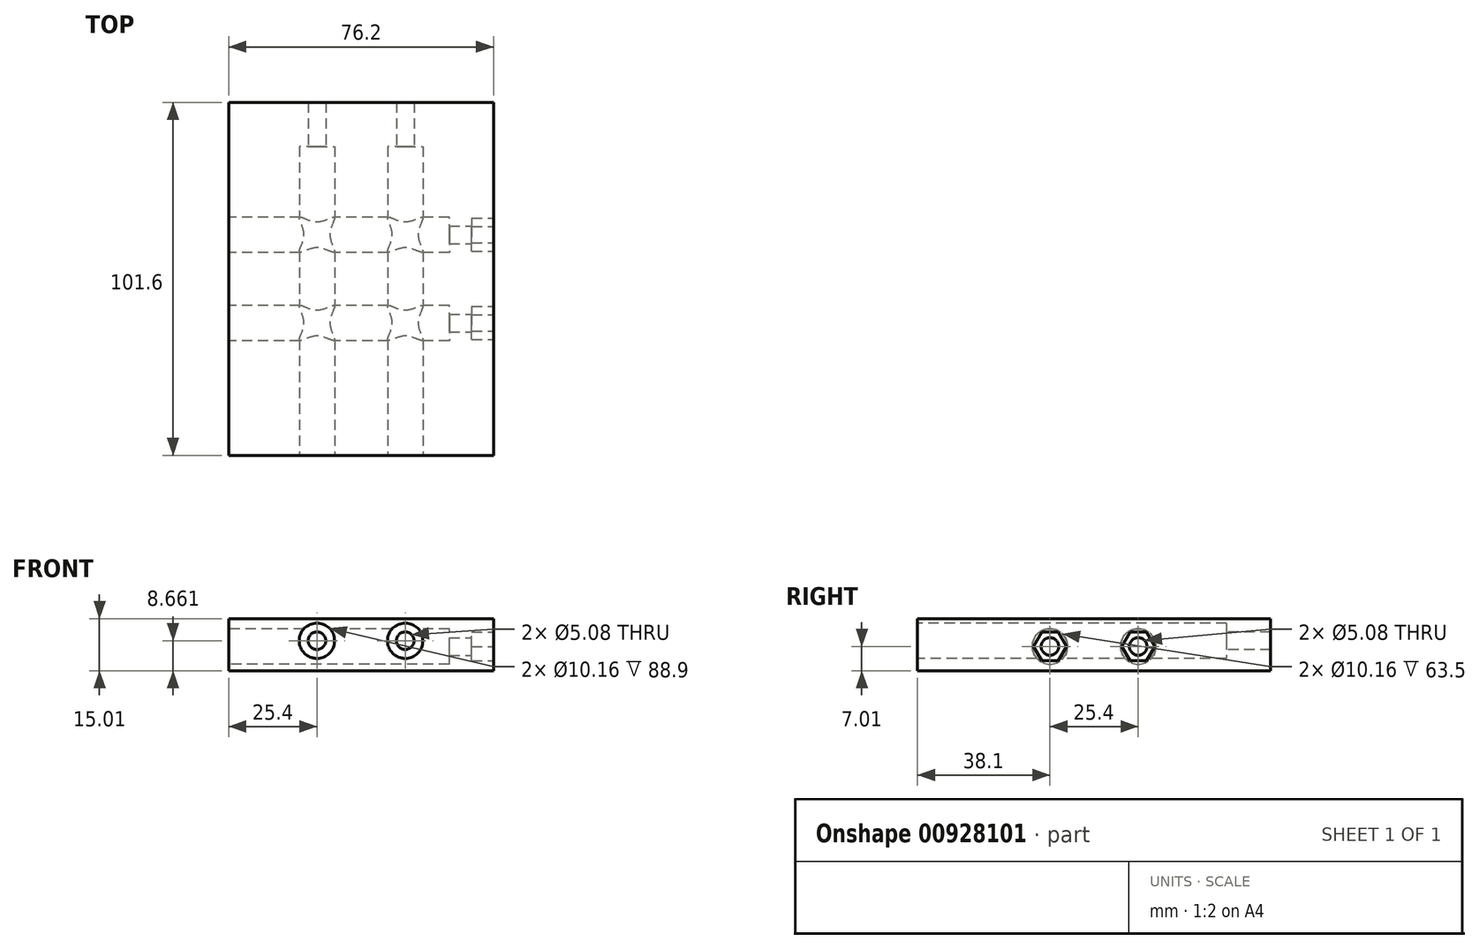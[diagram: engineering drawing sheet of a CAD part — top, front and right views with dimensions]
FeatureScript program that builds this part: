
annotation { "Feature Type Name" : "Feature", "Feature Type Description" : "" }
export const myFeature = defineFeature(function(context is Context, id is Id, definition is map)
    precondition{}
    {
        {
            var Q0;
            Q0=qCreatedBy(makeId("Top.planeOp"),FACE);
            var sketch = newSketch(context, id + "F0", { "sketchPlane" : qUnion([Q0])});
            skLineSegment(sketch, "E0.bottom", {"start": v(-38.1, 50.8) * mm, "end": v(38.1, 50.8) * mm});
            skLineSegment(sketch, "E0.top", {"start": v(-38.1, -50.8) * mm, "end": v(38.1, -50.8) * mm});
            skLineSegment(sketch, "E0.left", {"start": v(-38.1, 50.8) * mm, "end": v(-38.1, -50.8) * mm});
            skLineSegment(sketch, "E0.right", {"start": v(38.1, 50.8) * mm, "end": v(38.1, -50.8) * mm});
            skPoint(sketch, "E0.middle", {"position": v(0, 0) * mm});
            skSolve(sketch);
        }
        {
            var Q0;
            Q0 = qSketchRegion(id + "F0", true);
            extrude(context, id + "F1", {"entities" : qUnion([Q0]), "depth" : 15 * mm, "offsetDistance" : 25.4 * mm});
        }
        {
            var Q0;
            Q0=makeQuery(id+"F1.opExtrude","SWEPT_FACE",FACE,{"disambiguationData":[OSD([sQuery(id+"F0.wireOp",EDGE,"E0.top")])]});
            var sketch = newSketch(context, id + "F2", { "sketchPlane" : qUnion([Q0])});
            skCircle(sketch, "E1", {"center": v(-12.7, 8.66) * mm, "radius": 2.54 * mm});
            skCircle(sketch, "E2", {"center": v(12.7, 8.66) * mm, "radius": 2.54 * mm});
            skLineSegment(sketch, "E3", {"start": v(12.7, 8.66) * mm, "end": v(-12.7, 8.66) * mm, "construction": true});
            skLineSegment(sketch, "E4", {"start": v(0, 8.66) * mm, "end": v(0, 15.01) * mm, "construction": true});
            skPoint(sketch, "E4.startSnap0", {"position": v(0, 15.01) * mm});
            skPoint(sketch, "E4.endSnap0", {"position": v(0, 15.01) * mm});
            skSolve(sketch);
        }
        {
            var Q0;
            Q0 = qSketchRegion(id + "F2", true);
            extrude(context, id + "F3", {"entities" : qUnion([Q0]), "operationType" : NewBodyOperationType.REMOVE, "endBound" : BoundingType.THROUGH_ALL, "oppositeDirection" : true, "depth" : 25.4 * mm, "offsetDistance" : 25.4 * mm});
        }
        {
            var Q0;
            Q0=makeQuery(id+"F1.opExtrude","SWEPT_FACE",FACE,{"disambiguationData":[OSD([sQuery(id+"F0.wireOp",EDGE,"E0.top")])]});
            var sketch = newSketch(context, id + "F4", { "sketchPlane" : qUnion([Q0])});
            skCircle(sketch, "E5", {"center": v(-12.7, 8.66) * mm, "radius": 5.08 * mm});
            skCircle(sketch, "E6", {"center": v(12.7, 8.66) * mm, "radius": 5.08 * mm});
            skSolve(sketch);
        }
        {
            var Q0;
            Q0 = qSketchRegion(id + "F4", true);
            var Q1;
            Q1=makeQuery(id+"F1.opExtrude","SWEPT_FACE",FACE,{"disambiguationData":[OSD([sQuery(id+"F0.wireOp",EDGE,"E0.bottom")])]});
            extrude(context, id + "F5", {"entities" : qUnion([Q0]), "operationType" : NewBodyOperationType.REMOVE, "endBound" : BoundingType.UP_TO_SURFACE, "oppositeDirection" : true, "depth" : 25.4 * mm, "endBoundEntityFace" : qUnion([Q1]), "hasOffset" : true, "offsetDistance" : 12.7 * mm});
        }
        {
            var Q0;
            Q0=makeQuery(id+"F1.opExtrude","SWEPT_FACE",FACE,{"disambiguationData":[OSD([sQuery(id+"F0.wireOp",EDGE,"E0.right")])]});
            var sketch = newSketch(context, id + "F6", { "sketchPlane" : qUnion([Q0])});
            skCircle(sketch, "E7.cCircle", {"center": v(-12.7, 7.01) * mm, "radius": 4.11 * mm, "construction": true});
            skLineSegment(sketch, "E7.0", {"start": v(-17.45, 7.01) * mm, "end": v(-15.07, 11.12) * mm});
            skLineSegment(sketch, "E7.1", {"start": v(-15.07, 11.12) * mm, "end": v(-10.33, 11.12) * mm});
            skLineSegment(sketch, "E7.2", {"start": v(-10.33, 11.12) * mm, "end": v(-7.95, 7.01) * mm});
            skLineSegment(sketch, "E7.3", {"start": v(-7.95, 7.01) * mm, "end": v(-10.33, 2.9) * mm});
            skLineSegment(sketch, "E7.4", {"start": v(-10.33, 2.9) * mm, "end": v(-15.07, 2.9) * mm});
            skLineSegment(sketch, "E7.5", {"start": v(-15.07, 2.9) * mm, "end": v(-17.45, 7.01) * mm});
            skPoint(sketch, "E7.0.midPoint", {"position": v(-16.26, 9.07) * mm});
            skCircle(sketch, "E8.cCircle", {"center": v(12.7, 7.01) * mm, "radius": 4.11 * mm, "construction": true});
            skLineSegment(sketch, "E8.0", {"start": v(7.95, 7.01) * mm, "end": v(10.33, 11.12) * mm});
            skLineSegment(sketch, "E8.1", {"start": v(10.33, 11.12) * mm, "end": v(15.07, 11.12) * mm});
            skLineSegment(sketch, "E8.2", {"start": v(15.07, 11.12) * mm, "end": v(17.45, 7.01) * mm});
            skLineSegment(sketch, "E8.3", {"start": v(17.45, 7.01) * mm, "end": v(15.07, 2.9) * mm});
            skLineSegment(sketch, "E8.4", {"start": v(15.07, 2.9) * mm, "end": v(10.33, 2.9) * mm});
            skLineSegment(sketch, "E8.5", {"start": v(10.33, 2.9) * mm, "end": v(7.95, 7.01) * mm});
            skPoint(sketch, "E8.0.midPoint", {"position": v(9.14, 9.07) * mm});
            skLineSegment(sketch, "E9", {"start": v(-12.7, 7.01) * mm, "end": v(-12.7, 15.01) * mm, "construction": true});
            skPoint(sketch, "E9.endSnap0", {"position": v(-12.7, 11.12) * mm});
            skLineSegment(sketch, "E10", {"start": v(-12.7, 7.01) * mm, "end": v(-12.7, 0) * mm, "construction": true});
            skSolve(sketch);
        }
        {
            var Q0;
            Q0 = qSketchRegion(id + "F6", true);
            extrude(context, id + "F7", {"entities" : qUnion([Q0]), "operationType" : NewBodyOperationType.REMOVE, "oppositeDirection" : true, "depth" : 6.25 * mm, "offsetDistance" : 25.4 * mm});
        }
        {
            var Q0;
            Q0=makeQuery(id+"F7.boolean.opBoolean","COPY",FACE,{"derivedFrom":makeQuery(id+"F7.opExtrude","CAP_FACE",FACE,{"disambiguationData":[OSD([sQuery(id+"F6.wireOp",EDGE,"E7.0"),sQuery(id+"F6.wireOp",EDGE,"E7.1"),sQuery(id+"F6.wireOp",EDGE,"E7.2"),sQuery(id+"F6.wireOp",EDGE,"E7.3"),sQuery(id+"F6.wireOp",EDGE,"E7.4"),sQuery(id+"F6.wireOp",EDGE,"E7.5")])],"isStart":false})});
            var sketch = newSketch(context, id + "F8", { "sketchPlane" : qUnion([Q0])});
            skCircle(sketch, "E11", {"center": v(-12.7, 7.01) * mm, "radius": 2.54 * mm});
            skCircle(sketch, "E12", {"center": v(12.7, 7.01) * mm, "radius": 2.54 * mm});
            skSolve(sketch);
        }
        {
            var Q0;
            Q0 = qSketchRegion(id + "F8", true);
            extrude(context, id + "F9", {"entities" : qUnion([Q0]), "operationType" : NewBodyOperationType.REMOVE, "endBound" : BoundingType.THROUGH_ALL, "oppositeDirection" : true, "depth" : 25.4 * mm, "offsetDistance" : 25.4 * mm});
        }
        {
            var Q0;
            Q0=makeQuery(id+"F1.opExtrude","SWEPT_FACE",FACE,{"disambiguationData":[OSD([sQuery(id+"F0.wireOp",EDGE,"E0.left")])]});
            var sketch = newSketch(context, id + "F10", { "sketchPlane" : qUnion([Q0])});
            skCircle(sketch, "E13", {"center": v(-12.7, 7.01) * mm, "radius": 5.08 * mm});
            skCircle(sketch, "E14", {"center": v(12.7, 7.01) * mm, "radius": 5.08 * mm});
            skSolve(sketch);
        }
        {
            var Q0;
            Q0 = qSketchRegion(id + "F10", true);
            var Q1;
            Q1=makeQuery(id+"F1.opExtrude","SWEPT_FACE",FACE,{"disambiguationData":[OSD([sQuery(id+"F0.wireOp",EDGE,"E0.right")])]});
            extrude(context, id + "F11", {"entities" : qUnion([Q0]), "operationType" : NewBodyOperationType.REMOVE, "endBound" : BoundingType.UP_TO_SURFACE, "oppositeDirection" : true, "depth" : 25.4 * mm, "endBoundEntityFace" : qUnion([Q1]), "hasOffset" : true, "offsetDistance" : 12.7 * mm});
        }
    });
